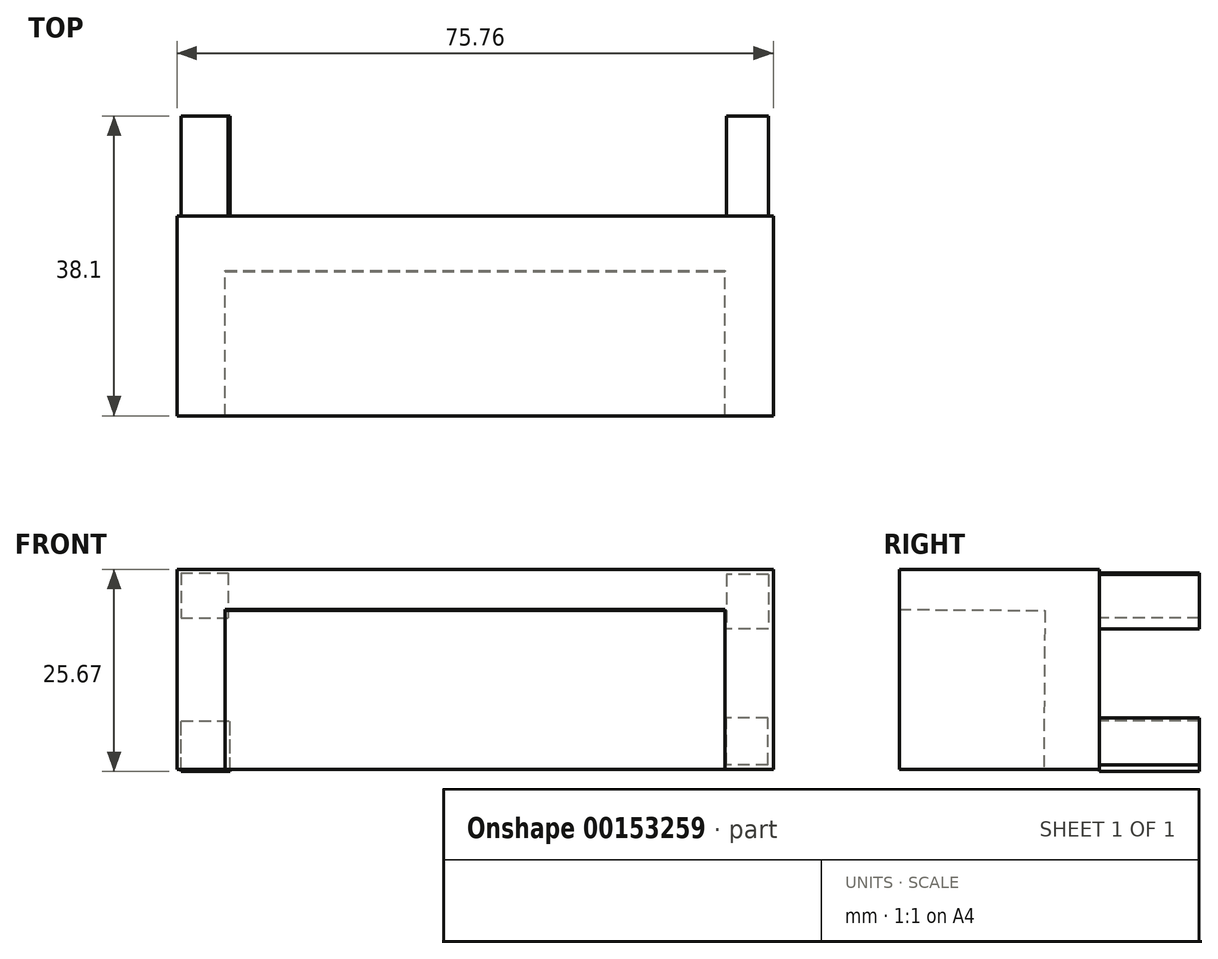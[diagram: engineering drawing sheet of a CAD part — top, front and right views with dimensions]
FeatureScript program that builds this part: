
annotation { "Feature Type Name" : "Feature", "Feature Type Description" : "" }
export const myFeature = defineFeature(function(context is Context, id is Id, definition is map)
    precondition{}
    {
        {
            var Q0;
            Q0=qCreatedBy(makeId("Front.planeOp"),FACE);
            var sketch = newSketch(context, id + "F0", { "sketchPlane" : qUnion([Q0])});
            skLineSegment(sketch, "E0.bottom", {"start": v(-37.88, 12.7) * mm, "end": v(37.88, 12.7) * mm});
            skLineSegment(sketch, "E0.top", {"start": v(-37.88, -12.7) * mm, "end": v(37.88, -12.7) * mm});
            skLineSegment(sketch, "E0.left", {"start": v(-37.88, 12.7) * mm, "end": v(-37.88, -12.7) * mm});
            skLineSegment(sketch, "E0.right", {"start": v(37.88, 12.7) * mm, "end": v(37.88, -12.7) * mm});
            skPoint(sketch, "E0.middle", {"position": v(0, 0) * mm});
            skSolve(sketch);
        }
        {
            var Q0;
            Q0=makeQuery(id+"F0.imprint","IMPRINT",FACE,{"disambiguationData":[TD([[makeQuery(id+"F0.imprint","IMPRINT",EDGE,{"derivedFrom":sQuery(id+"F0.wireOp",EDGE,"E0.bottom")}),-1.0]])]});
            extrude(context, id + "F1", {"entities" : qUnion([Q0]), "depth" : 25.4 * mm});
        }
        {
            var Q0;
            Q0=qCreatedBy(makeId("Right.planeOp"),FACE);
            var sketch = newSketch(context, id + "F2", { "sketchPlane" : qUnion([Q0])});
            skLineSegment(sketch, "E1", {"start": v(-35.07, 7.68) * mm, "end": v(-6.91, 7.49) * mm});
            skLineSegment(sketch, "E2", {"start": v(-6.91, 7.49) * mm, "end": v(-7.13, -25.23) * mm});
            skLineSegment(sketch, "E3", {"start": v(-7.13, -25.23) * mm, "end": v(-39.28, -27.77) * mm});
            skLineSegment(sketch, "E4", {"start": v(-39.28, -27.77) * mm, "end": v(-35.07, 7.68) * mm});
            skSolve(sketch);
        }
        {
            var Q0;
            Q0=makeQuery(id+"F2.imprint","IMPRINT",FACE,{"disambiguationData":[TD([[makeQuery(id+"F2.imprint","IMPRINT",EDGE,{"derivedFrom":sQuery(id+"F2.wireOp",EDGE,"E1")}),-1.0]])]});
            extrude(context, id + "F3", {"entities" : qUnion([Q0]), "operationType" : NewBodyOperationType.REMOVE, "endBound" : BoundingType.SYMMETRIC, "oppositeDirection" : true, "depth" : 63.5 * mm});
        }
        {
            var Q0;
            Q0=qCreatedBy(makeId("Front.planeOp"),FACE);
            var sketch = newSketch(context, id + "F4", { "sketchPlane" : qUnion([Q0])});
            skLineSegment(sketch, "E5.bottom", {"start": v(-37.36, -12.97) * mm, "end": v(-31.14, -12.97) * mm});
            skLineSegment(sketch, "E5.top", {"start": v(-37.36, -6.53) * mm, "end": v(-31.14, -6.53) * mm});
            skLineSegment(sketch, "E5.left", {"start": v(-37.36, -12.97) * mm, "end": v(-37.36, -6.53) * mm});
            skLineSegment(sketch, "E5.right", {"start": v(-31.14, -12.97) * mm, "end": v(-31.14, -6.53) * mm});
            skPoint(sketch, "E5.middle", {"position": v(-34.25, -9.75) * mm});
            skLineSegment(sketch, "E6.bottom", {"start": v(-37.38, 12.25) * mm, "end": v(-31.4, 12.25) * mm});
            skLineSegment(sketch, "E6.top", {"start": v(-37.38, 6.55) * mm, "end": v(-31.4, 6.55) * mm});
            skLineSegment(sketch, "E6.left", {"start": v(-37.38, 12.25) * mm, "end": v(-37.38, 6.55) * mm});
            skLineSegment(sketch, "E6.right", {"start": v(-31.4, 12.25) * mm, "end": v(-31.4, 6.55) * mm});
            skPoint(sketch, "E6.middle", {"position": v(-34.39, 9.4) * mm});
            skLineSegment(sketch, "E7.bottom", {"start": v(37.17, -12.13) * mm, "end": v(31.95, -12.13) * mm});
            skLineSegment(sketch, "E7.top", {"start": v(37.17, -6.16) * mm, "end": v(31.95, -6.16) * mm});
            skLineSegment(sketch, "E7.left", {"start": v(37.17, -12.13) * mm, "end": v(37.17, -6.16) * mm});
            skLineSegment(sketch, "E7.right", {"start": v(31.95, -12.13) * mm, "end": v(31.95, -6.16) * mm});
            skPoint(sketch, "E7.middle", {"position": v(34.56, -9.15) * mm});
            skLineSegment(sketch, "E8.bottom", {"start": v(37.25, 12.06) * mm, "end": v(31.92, 12.06) * mm});
            skLineSegment(sketch, "E8.top", {"start": v(37.25, 5.14) * mm, "end": v(31.92, 5.14) * mm});
            skLineSegment(sketch, "E8.left", {"start": v(37.25, 12.06) * mm, "end": v(37.25, 5.14) * mm});
            skLineSegment(sketch, "E8.right", {"start": v(31.92, 12.06) * mm, "end": v(31.92, 5.14) * mm});
            skPoint(sketch, "E8.middle", {"position": v(34.58, 8.6) * mm});
            skSolve(sketch);
        }
        {
            var Q0;
            Q0=makeQuery(id+"F4.imprint","IMPRINT",FACE,{"disambiguationData":[TD([[makeQuery(id+"F4.imprint","IMPRINT",EDGE,{"derivedFrom":sQuery(id+"F4.wireOp",EDGE,"E6.bottom")}),-1.0]])]});
            var Q1;
            Q1=makeQuery(id+"F4.imprint","IMPRINT",FACE,{"disambiguationData":[TD([[makeQuery(id+"F4.imprint","IMPRINT",EDGE,{"derivedFrom":sQuery(id+"F4.wireOp",EDGE,"E5.bottom")}),1.0]])]});
            var Q2;
            Q2=makeQuery(id+"F4.imprint","IMPRINT",FACE,{"disambiguationData":[TD([[makeQuery(id+"F4.imprint","IMPRINT",EDGE,{"derivedFrom":sQuery(id+"F4.wireOp",EDGE,"E7.bottom")}),-1.0]])]});
            var Q3;
            Q3=makeQuery(id+"F4.imprint","IMPRINT",FACE,{"disambiguationData":[TD([[makeQuery(id+"F4.imprint","IMPRINT",EDGE,{"derivedFrom":sQuery(id+"F4.wireOp",EDGE,"E8.bottom")}),1.0]])]});
            extrude(context, id + "F5", {"entities" : qUnion([Q0, Q1, Q2, Q3]), "operationType" : NewBodyOperationType.ADD, "oppositeDirection" : true, "depth" : 12.7 * mm});
        }
    });
